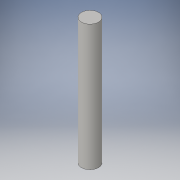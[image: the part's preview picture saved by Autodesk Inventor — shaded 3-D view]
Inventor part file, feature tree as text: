
AUTODESK INVENTOR PART (.ipt)
format: ipt  version: 2016 (Build 200138000, 138)  size: 84,480 bytes
history: native  units: in
note: dims shown in document units (in); Inventor stores cm internally (conversion verified against a paired STEP export)
features: extrude x1, sketch x1
ambient origin geometry x8: Origin, YZ Plane, XZ Plane, XY Plane, X Axis, Y Axis, Z Axis, Center Point
bodies: Solid1 (feature_tree)
feature tree (2):
  extrude  "Extrusion1"  Depth=1.75in TaperAngle=0.0deg
  sketch  "Sketch1"  dims[d0=0.2362in d1=1.75in d2=0.0in]
